# Revit family: NLRS_00_AIR_Muurrooster_ST-483_Storax
name_source: partatom
category: Air Terminals
units: mm (PartAtom-declared; Revit-internal decimal feet)

## family parameters
Cut with Voids When Loaded = No
Host = Face
Part Type = Normal
Room Calculation Point = Yes
Round Connector Dimension = Use Diameter
Shared = No

## types (1)
- ST-483
    Apparent Load = 0 VA
    Assembly Code = 57.10.90.1
    Based on = Renson
    Default Elevation = 1219 mm
    Description = ST-483
    Export Type to IFC As = IfcAirTerminalType
    IfcExportAs = IfcAirTerminalType
    IfcExportType = Grille
    Manufacturer = Storax
    Model = ST-483
    RSen_C_code_CBNL = Louvre
    RSen_C_code_ETIM = Overstroomrooster
    RSen_C_code_ETIM_URL = https://www.storax.nl
    RSen_C_code_article = ST-483
    RSen_C_code_gtin = -
    RSen_C_depth = 87 mm  [stored 0.285433 ft]
    RSen_C_description = ST-483
    RSen_C_material = RSen_h4_aluminum
    RSen_C_model = ST-483
    RSen_C_type = high-airflow
    RSen_C_type_comments = glazed-in louvre
    STX_I Backframe = No
    STX_I Backframe_max wall thickness = 0 mm  [stored 0 ft]
    STX_I Backframe_min wall thickness = 0 mm  [stored 0 ft]
    STX_I BaseKeynote = 57.10.90.1
    STX_I Blade_pitch = 60 mm  [stored 0.19685 ft]
    STX_I Blade_shape = Z
    STX_I Blade_type = L.060HF
    STX_I Burglarproof_RC class = -
    STX_I Cd coefficient_discharge = 0.422
    STX_I Ce coefficient_intake = 0.423
    STX_I Control = -
    STX_I Depth_max = 0 mm  [stored 0 ft]
    STX_I Depth_min = 0 mm  [stored 0 ft]
    STX_I Diameter_max = 0 mm  [stored 0 ft]
    STX_I Diameter_min = 0 mm  [stored 0 ft]
    STX_I Drainage profile = Yes
    STX_I Fire resistance = -
    STX_I Flange_height = 40 mm  [stored 0.131234 ft]
    STX_I Flange_thickness = 24 mm  [stored 0.0787402 ft]
    STX_I Flange_thickness max = 32 mm  [stored 0.104987 ft]
    STX_I Flange_thickness min = 24 mm  [stored 0.0787402 ft]
    STX_I G4 filter = Yes
    STX_I Glazed in = Yes
    STX_I Height_max = 4000 mm  [stored 13.1234 ft]
    STX_I Height_min = 385 mm  [stored 1.26312 ft]
    STX_I IP = -
    STX_I K factor_discharge = 5.62
    STX_I K factor_intake = 5.59
    STX_I Material = aluminiumAlMgSi0.5
    STX_I Puncture proof = No
    STX_I Removable insect mesh = Yes
    STX_I Removable insect mesh_info = Min. dimensions: 190x190 mm; Max. dimensions: 1500x1200 mm
    STX_I Shape = rectangular
    STX_I Size_maximum = see price list
    STX_I Sound reduction_Dw = -
    STX_I Sound reduction_Rw = -
    STX_I U-value = -
    STX_I Visual free area = 0.9
    STX_I Water channel = Yes
    STX_I Width_max = 4000 mm  [stored 13.1234 ft]
    STX_I Width_min = 385 mm  [stored 1.26312 ft]
    STX_I Without flange = No
    STX_I Without flange_info = no
    STX_I Zichtbaar vrije opp. = 0.76
    STX_V Air exhaust = No
    STX_V Supply air = Yes
    STX_W Fingerprint = <RSen_C_length> x <RSen_C_height> mm
    Type Comments = glazed-in louvre
    Type IFC Predefined Type = Grille
    ZZZ_Airflow_HVACAirflow = 1.0 m³/h
    ZZZ_Cut out_depth negative_Length = -500 mm  [stored -1.64042 ft]
    ZZZ_Cut out_depth_Length = 500 mm  [stored 1.64042 ft]
    ZZZ_Depth negative_Length = -87 mm  [stored -0.285433 ft]
    ZZZ_Depth_Length = 87 mm  [stored 0.285433 ft]
    ZZZ_Flange_FamilyType_Air Terminals = GEO_flange - gl_renson : standard
    ZZZ_Flange_offset_Length = 58 mm  [stored 0.190289 ft]
    ZZZ_Housing_medium and coarse_FamilyType_Air Terminals = GEO_housing - gl - medium and coarse_renson : standard
    ZZZ_Louvre_FamilyType_Air Terminals = GEO_louvre_renson : standard
    ZZZ_Louvre_insertion point negative_Length = 0 mm  [stored 0 ft]
    ZZZ_Louvre_insertion point_Length = 0 mm  [stored 0 ft]
    ZZZ_Profile bottom_minimum height_Length = 60 mm  [stored 0.19685 ft]
    ZZZ_Profile middle_offset_Length = 60 mm  [stored 0.19685 ft]
    ZZZ_Profile top_offset_Length = 125 mm  [stored 0.410105 ft]

note: [stored X ft] marks values corroborated as IEEE doubles in the binary element streams (Revit-internal decimal feet)

## geometry (parser evidence)
native form markers: Sweep x70
no freeform markers — native parametric forms only
